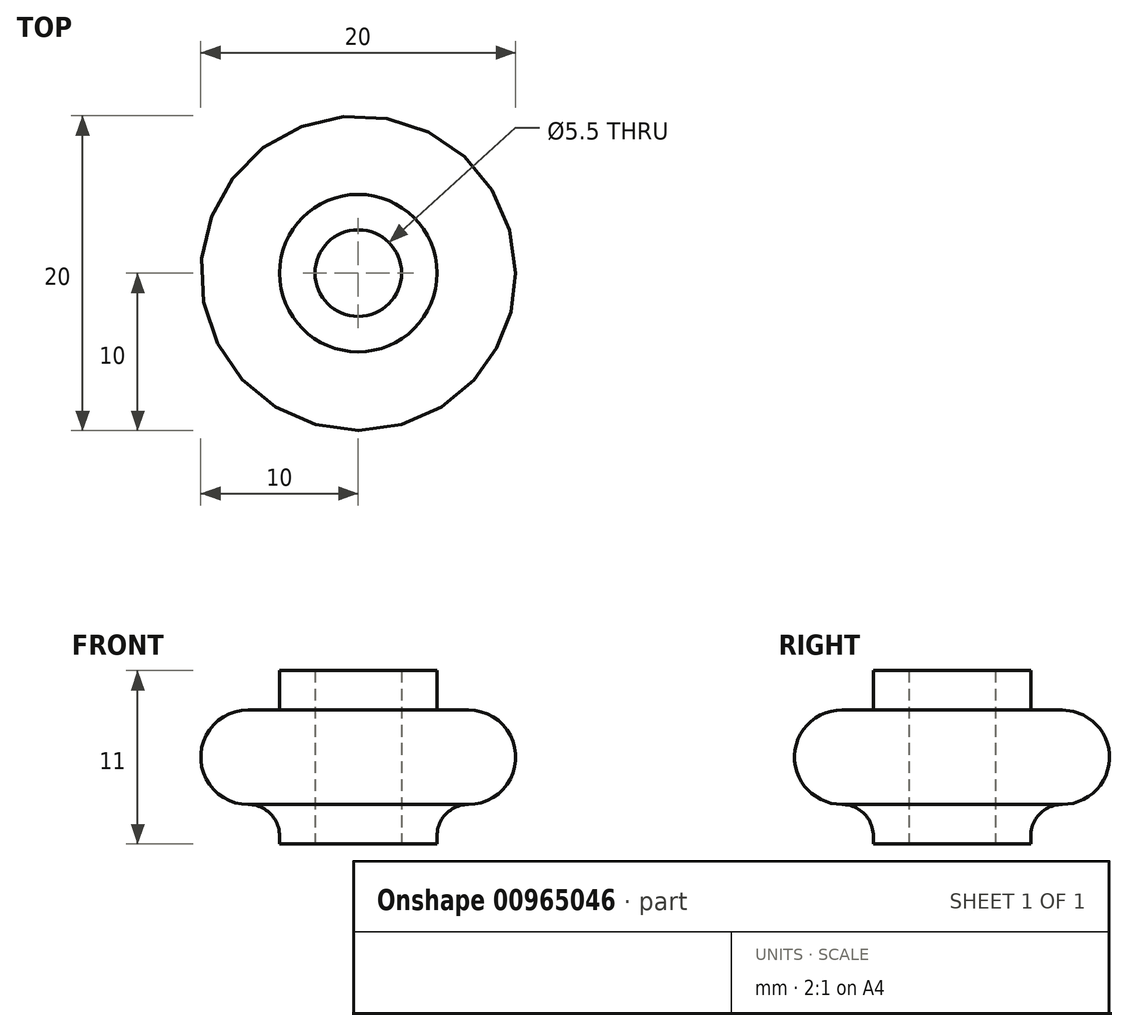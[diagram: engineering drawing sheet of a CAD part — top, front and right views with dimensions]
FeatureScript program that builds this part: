
annotation { "Feature Type Name" : "Feature", "Feature Type Description" : "" }
export const myFeature = defineFeature(function(context is Context, id is Id, definition is map)
    precondition{}
    {
        {
            var Q0;
            Q0=qCreatedBy(makeId("Top.planeOp"),FACE);
            var sketch = newSketch(context, id + "F0", { "sketchPlane" : qUnion([Q0])});
            skCircle(sketch, "E0", {"center": v(0, 0) * mm, "radius": 2.75 * mm});
            skCircle(sketch, "E1", {"center": v(0, 0) * mm, "radius": 10 * mm});
            skCircle(sketch, "E2", {"center": v(0, 0) * mm, "radius": 5 * mm});
            skSolve(sketch);
        }
        {
            var Q0;
            Q0=makeQuery(id+"F0.imprint","IMPRINT",FACE,{"disambiguationData":[TD([[makeQuery(id+"F0.imprint","IMPRINT",EDGE,{"derivedFrom":sQuery(id+"F0.wireOp",EDGE,"E0")}),-1.0]])]});
            extrude(context, id + "F1", {"entities" : qUnion([Q0]), "endBound" : BoundingType.SYMMETRIC, "depth" : 11 * mm, "offsetDistance" : 25 * mm});
        }
        {
            var Q0;
            Q0=makeQuery(id+"F0.imprint","IMPRINT",FACE,{"disambiguationData":[TD([[makeQuery(id+"F0.imprint","IMPRINT",EDGE,{"derivedFrom":sQuery(id+"F0.wireOp",EDGE,"E1")}),1.0]])]});
            extrude(context, id + "F2", {"entities" : qUnion([Q0]), "operationType" : NewBodyOperationType.ADD, "endBound" : BoundingType.SYMMETRIC, "depth" : 6 * mm, "offsetDistance" : 25 * mm});
        }
        {
            var Q0;
            Q0=makeQuery(id+"F2.opExtrude","CAP_EDGE",EDGE,{"disambiguationData":[OSD([sQuery(id+"F0.wireOp",EDGE,"E1")])],"isStart":false});
            var Q1;
            Q1=makeQuery(id+"F2.opExtrude","CAP_EDGE",EDGE,{"disambiguationData":[OSD([sQuery(id+"F0.wireOp",EDGE,"E1")])],"isStart":true});
            fillet(context, id + "F3", {"entities" : qUnion([Q0, Q1]), "tangentPropagation" : true, "radius" : 3 * mm, "defaultsChanged" : true, "vertexSettings" : [], "allowEdgeOverflow" : false});
        }
        {
            var Q0;
            Q0=makeQuery(id+"F2.opExtrude","CAP_EDGE",EDGE,{"disambiguationData":[OSD([sQuery(id+"F0.wireOp",EDGE,"E2")])],"isStart":false});
            var Q1;
            Q1=makeQuery(id+"F2.opExtrude","CAP_EDGE",EDGE,{"disambiguationData":[OSD([sQuery(id+"F0.wireOp",EDGE,"E2")])],"isStart":true});
            fillet(context, id + "F4", {"entities" : qUnion([Q0, Q1]), "tangentPropagation" : true, "radius" : 2 * mm, "defaultsChanged" : true, "vertexSettings" : [], "allowEdgeOverflow" : false});
        }
    });
